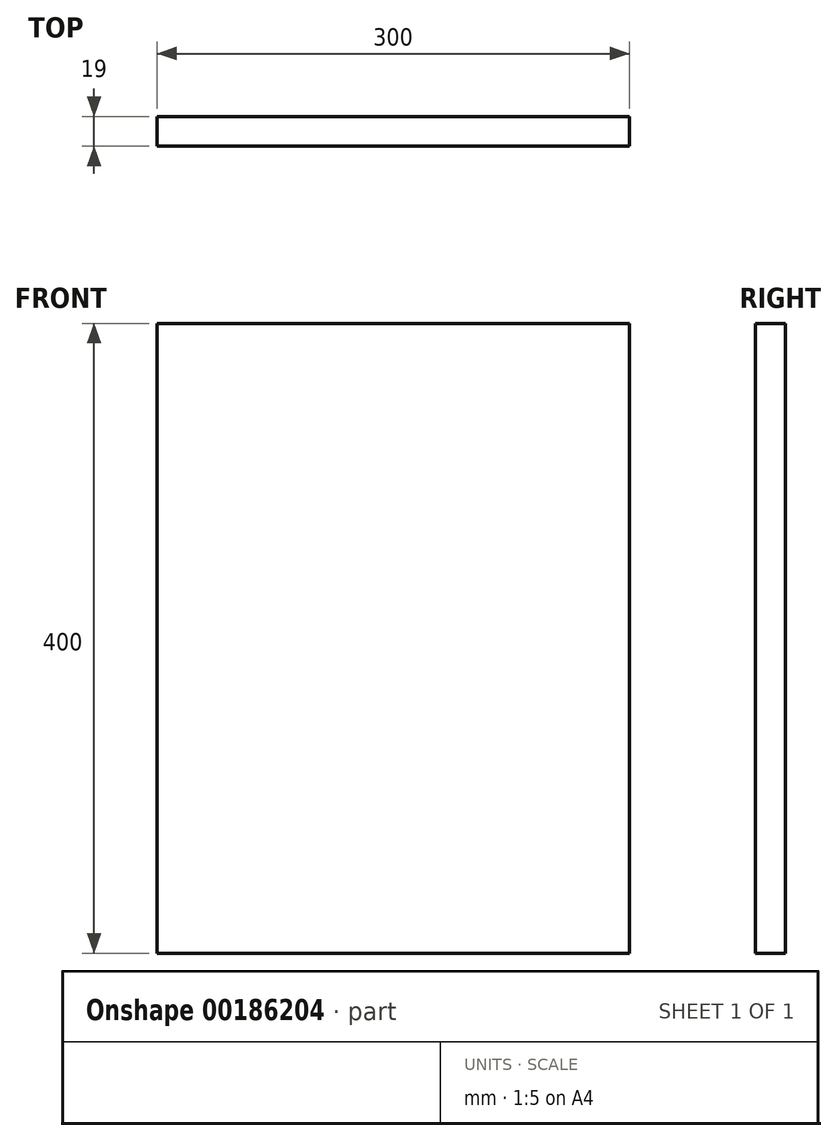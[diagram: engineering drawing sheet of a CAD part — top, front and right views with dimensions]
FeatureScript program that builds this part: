
annotation { "Feature Type Name" : "Feature", "Feature Type Description" : "" }
export const myFeature = defineFeature(function(context is Context, id is Id, definition is map)
    precondition{}
    {
        {
            var Q0;
            Q0=qCreatedBy(makeId("Front.planeOp"),FACE);
            var sketch = newSketch(context, id + "F0", { "sketchPlane" : qUnion([Q0])});
            skLineSegment(sketch, "E0.bottom", {"start": v(-156.19, 230.1) * mm, "end": v(143.81, 230.1) * mm});
            skLineSegment(sketch, "E0.top", {"start": v(-156.19, -169.9) * mm, "end": v(143.81, -169.9) * mm});
            skLineSegment(sketch, "E0.left", {"start": v(-156.19, 230.1) * mm, "end": v(-156.19, -169.9) * mm});
            skLineSegment(sketch, "E0.right", {"start": v(143.81, 230.1) * mm, "end": v(143.81, -169.9) * mm});
            skSolve(sketch);
        }
        {
            var Q0;
            Q0 = qSketchRegion(id + "F0", true);
            extrude(context, id + "F1", {"entities" : qUnion([Q0]), "depth" : 19 * mm});
        }
    });
